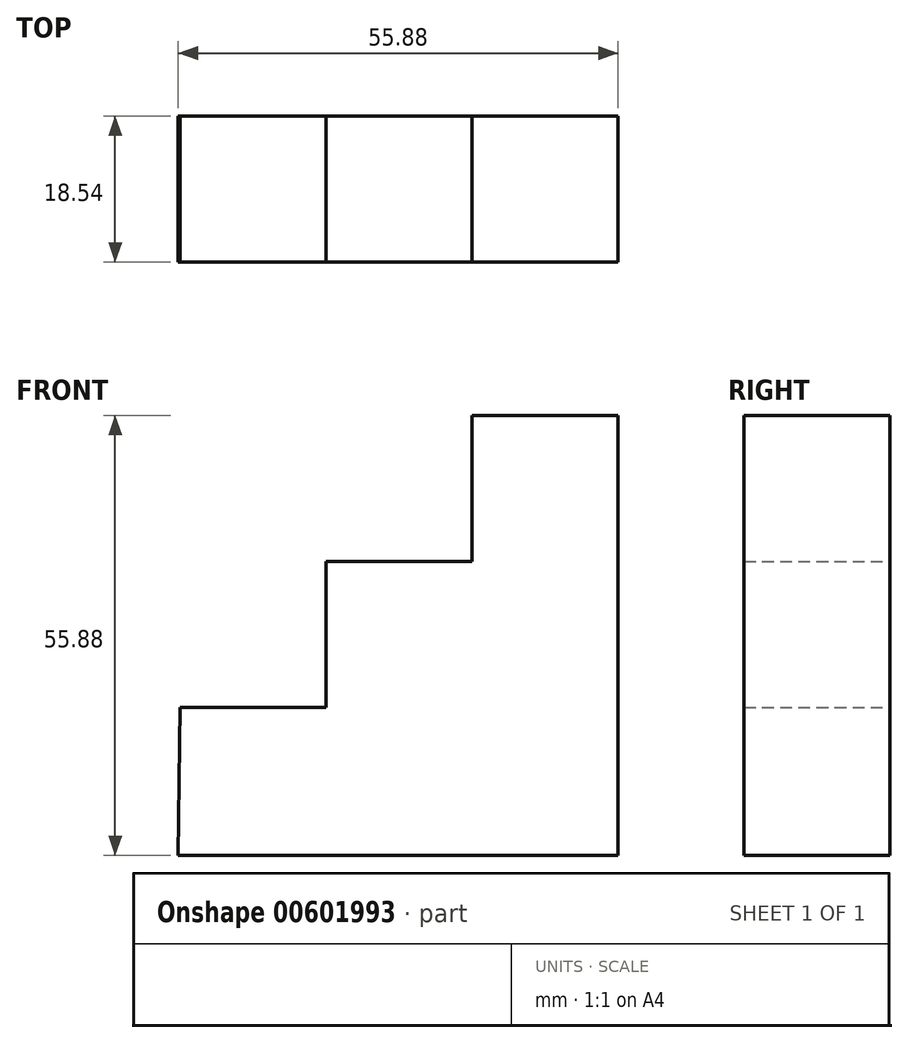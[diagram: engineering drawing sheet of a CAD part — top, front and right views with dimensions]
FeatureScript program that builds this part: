
annotation { "Feature Type Name" : "Feature", "Feature Type Description" : "" }
export const myFeature = defineFeature(function(context is Context, id is Id, definition is map)
    precondition{}
    {
        {
            var Q0;
            Q0=qCreatedBy(makeId("Front.planeOp"),FACE);
            var sketch = newSketch(context, id + "F0", { "sketchPlane" : qUnion([Q0])});
            skLineSegment(sketch, "E0", {"start": v(-19.84, -19.36) * mm, "end": v(36.04, -19.36) * mm});
            skLineSegment(sketch, "E1", {"start": v(36.04, -19.36) * mm, "end": v(36.04, 36.52) * mm});
            skLineSegment(sketch, "E2", {"start": v(36.04, 36.52) * mm, "end": v(17.5, 36.52) * mm});
            skLineSegment(sketch, "E3", {"start": v(17.5, 36.52) * mm, "end": v(17.5, 17.98) * mm});
            skLineSegment(sketch, "E4", {"start": v(17.5, 17.98) * mm, "end": v(-1.04, 17.98) * mm});
            skLineSegment(sketch, "E5", {"start": v(-1.04, 17.98) * mm, "end": v(-1.04, -0.56) * mm});
            skLineSegment(sketch, "E6", {"start": v(-1.04, -0.56) * mm, "end": v(-19.59, -0.56) * mm});
            skLineSegment(sketch, "E7", {"start": v(-19.59, -0.56) * mm, "end": v(-19.84, -19.36) * mm});
            skSolve(sketch);
        }
        {
            var Q0;
            Q0=makeQuery(id+"F0.imprint","IMPRINT",FACE,{"disambiguationData":[TD([[makeQuery(id+"F0.imprint","IMPRINT",EDGE,{"derivedFrom":sQuery(id+"F0.wireOp",EDGE,"E0")}),1.0]])]});
            extrude(context, id + "F1", {"entities" : qUnion([Q0]), "depth" : 18.54 * mm, "offsetDistance" : 25 * mm});
        }
    });
